# Revit family: ВК-ВО
name_source: partatom
category: Арматура воздуховодов
units: mm (PartAtom-declared; Revit-internal decimal feet)

## family parameters
Всегда вертикально = Да
На основе рабочей плоскости = Нет
Общий = Нет
При загрузке вырезать с полостями = Нет
Размер круглого соединителя = Использовать диаметр
Тип детали = Присоединяется

## types (11) — shared parameters
00_20_Виробник = Вентс
00_20_Назва = Вхідний конус
URL = https://vents.ua
Изготовитель = Вентс
Класифікація навантаження = HVAC
Матеріал зони обслуговуваня = <По категории>
Матеріал корпусу = Метал, пофарбований, синій, матовий RAL 5007
zero-valued in all types: Отметка по умолчанию

## per-type parameters (varying)
| type | D | D1 | D2 | F | F1 | F2 | H | R | R1 | R2 | d | f | f1 | f2 | n | Вага | Довжина | Діаметр |
| ВК-ВО-400 | 400 мм | 450 мм | 490 мм | 450 мм | 500 мм | 540 мм | 95 мм | 200 мм | 225 мм | 245 мм | 8 мм | 225 мм | 250 мм | 270 мм | 12 | 2.70 кг | 95 мм | 540 мм |
| ВК-ВО-1250 | 1250 мм | 1320 мм | 1400 мм | 1400 мм | 1470 мм | 1550 мм | 285 мм | 625 мм | 660 мм | 700 мм | 15 мм | 700 мм | 735 мм | 775 мм | 20 | 53.50 кг | 285 мм | 1550 мм |
| ВК-ВО-450 | 450 мм | 500 мм | 540 мм | 500 мм | 560 мм | 600 мм | 110 мм | 225 мм | 250 мм | 270 мм | 8 мм | 250 мм | 280 мм | 300 мм | 12 | 3.30 кг | 110 мм | 600 мм |
| ВК-ВО-500 | 500 мм | 560 мм | 600 мм | 560 мм | 620 мм | 660 мм | 120 мм | 250 мм | 280 мм | 300 мм | 12 мм | 280 мм | 310 мм | 330 мм | 12 | 4.00 кг | 120 мм | 660 мм |
| ВК-ВО-560 | 560 мм | 620 мм | 660 мм | 630 мм | 690 мм | 730 мм | 135 мм | 280 мм | 310 мм | 330 мм | 12 мм | 315 мм | 345 мм | 365 мм | 12 | 4.65 кг | 135 мм | 730 мм |
| ВК-ВО-630 | 630 мм | 690 мм | 730 мм | 710 мм | 770 мм | 810 мм | 150 мм | 315 мм | 345 мм | 365 мм | 12 мм | 355 мм | 385 мм | 405 мм | 12 | 6.80 кг | 150 мм | 810 мм |
| ВК-ВО-710 | 710 мм | 770 мм | 810 мм | 800 мм | 860 мм | 900 мм | 170 мм | 355 мм | 385 мм | 405 мм | 12 мм | 400 мм | 430 мм | 450 мм | 16 | 12.00 кг | 170 мм | 900 мм |
| ВК-ВО-800 | 800 мм | 860 мм | 900 мм | 900 мм | 970 мм | 1015 мм | 190 мм | 400 мм | 430 мм | 450 мм | 12 мм | 450 мм | 485 мм | 508 мм | 16 | 15.00 кг | 190 мм | 1015 мм |
| ВК-ВО-900 | 900 мм | 970 мм | 1015 мм | 1000 мм | 1070 мм | 1115 мм | 210 мм | 450 мм | 485 мм | 508 мм | 15 мм | 500 мм | 535 мм | 558 мм | 16 | 21.00 кг | 210 мм | 1115 мм |
| ВК-ВО-1000 | 1000 мм | 1070 мм | 1115 мм | 1120 мм | 1190 мм | 1270 мм | 240 мм | 500 мм | 535 мм | 558 мм | 15 мм | 560 мм | 595 мм | 635 мм | 16 | 36.70 кг | 240 мм | 1270 мм |
| ВК-ВО-1120 | 1120 мм | 1190 мм | 1270 мм | 1250 мм | 1320 мм | 1400 мм | 255 мм | 560 мм | 595 мм | 635 мм | 15 мм | 625 мм | 660 мм | 700 мм | 20 | 45.00 кг | 255 мм | 1400 мм |

note: column(s) folded — value = type name in every type: 00_20_Тип
